# Revit family: Gira_107900
name_source: partatom
category: Elektroinstallationen
revit_build: Autodesk Revit 2017 (Build: 20160225_1515(x64)
units: mm (PartAtom-declared; Revit-internal decimal feet)

## family parameters
Basisbauteil = Fläche
Beim Laden mit Abzugskörper schneiden = Nein
Bemaßung runder Anschluss = Durchmesser verwenden
Beschriftungsausrichtung beibehalten = Nein
Gemeinsam genutzt = Nein
Raumberechnungspunkt = Nein
Teiletyp = Normal

## types (1)
- Spannungsversorgung 640 mA o.Drossel KNX REG
    Andere Bussysteme = ohne
    Anzahl der integrierten Drosseln = 0
    BIM = https://media.stage.bim.site 16f.rfa
    BIMSITE_PRODUCT_ID = dcdc9d8b2239130fc9737134f1ddaba9afbbed0b
    Beschreibung = KNX Spannungsversorgung 640 mA unterbrechungsfrei  REG Merkmale:  Die unterbrechungsfreie Spannungsversorgung 640 mA erzeugt die KNX Systemspannung.  Mit integrierter Drossel zur Entkopplung der Buslinie von der Spannungsversorgung.  Mit Anschlüssen für einen Bleigelakku zur Pufferung der KNX Spannung bei Netzausfall.  Es können bis zu zwei Bleigelakkumulatoren angeschlossen und über die unterbrechungsfreie Spannungsversorgung geladen werden.  Mit einem Temperaturfühler wird die Ladespannung temperaturabhängig geregelt.  Die unterbrechungsfreie Spannungsversorgung besitzt einen potenzialfreien Wechselkontakt zum Melden einer Störung (z. B. Netzausfall, Akku-Fehler, Überlast bzw. Kurzschluss).  Hinweise :  Der Anschluss erfolgt über KNX Busanschluss- bzw. Abzweigklemmen (keine Datenschiene erforderlich).  Empfehlung: Überspannungsschutz für Gira KNX Produkte.  Überspannungsableiter BUStector BT 24, Fabrikat: DEHN + SÖHNE, Artikel-Nr. 925001.
    Breite in Teilungseinheiten = 8
    Busspannung pufferbar = Ja
    Bussystem Funkbus = Nein
    Bussystem KNX = Ja
    Bussystem KNX-Funk = Nein
    Bussystem LON = Nein
    Bussystem Powernet = Nein
    Datenblatt = https://media.stage.bim.site
    Datenblatt 1 = https://media.stage.bim.site
    GTIN = 4010337009115
    HAN = 107900
    HeinzeBIM = https://www.heinze.de
    Hersteller = Gira
    Kosten = 0 $
    Max. Ausgangsstrom = 1 A
    Mit LED-Anzeige = Nein
    Montageart = REG
    Produktseite = https://media.stage.bim.site
    Typname = Spannungsversorgung 640 mA o.Drossel KNX REG
    URL = https://www.gira.de
    Vorgabe-Ansicht = 1219 mm

## geometry (parser evidence)
native form markers: Sweep x3
no freeform markers — native parametric forms only
